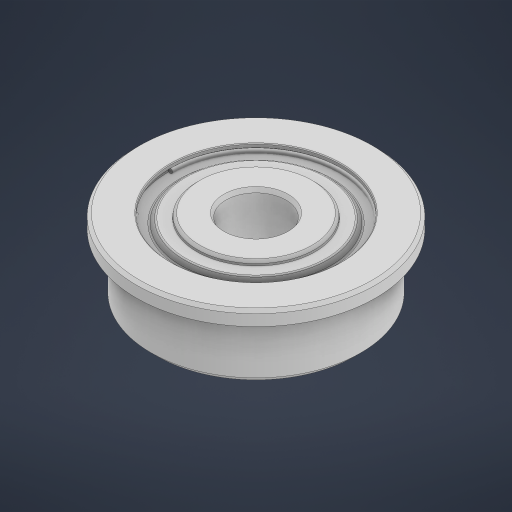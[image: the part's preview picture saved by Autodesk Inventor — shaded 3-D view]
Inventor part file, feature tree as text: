
AUTODESK INVENTOR PART (.ipt)
format: ipt  version: 2023 (Build 270158000, 158)  size: 336,896 bytes
history: native  units: in
note: dims shown in document units (in); Inventor stores cm internally (conversion verified against a paired STEP export)
features: revolve x1, mirror x1, chamfer x1
ambient origin geometry x8: Origin, YZ Plane, XZ Plane, XY Plane, X Axis, Y Axis, Z Axis, Center Point
bodies: Solid1 (feature_tree), Solid2 (feature_tree), Solid3 (feature_tree)
feature tree (3):
  revolve  "Revolve1"  [1 undecoded]
  mirror  "Mirror3"
  chamfer  "Chamfer7"  [1 undecoded]
note: 2 required parameter values undecoded (feature->parameter linkage not recoverable at this tier; creation-order binding heuristic only, values carry confidence <= 0.55)
